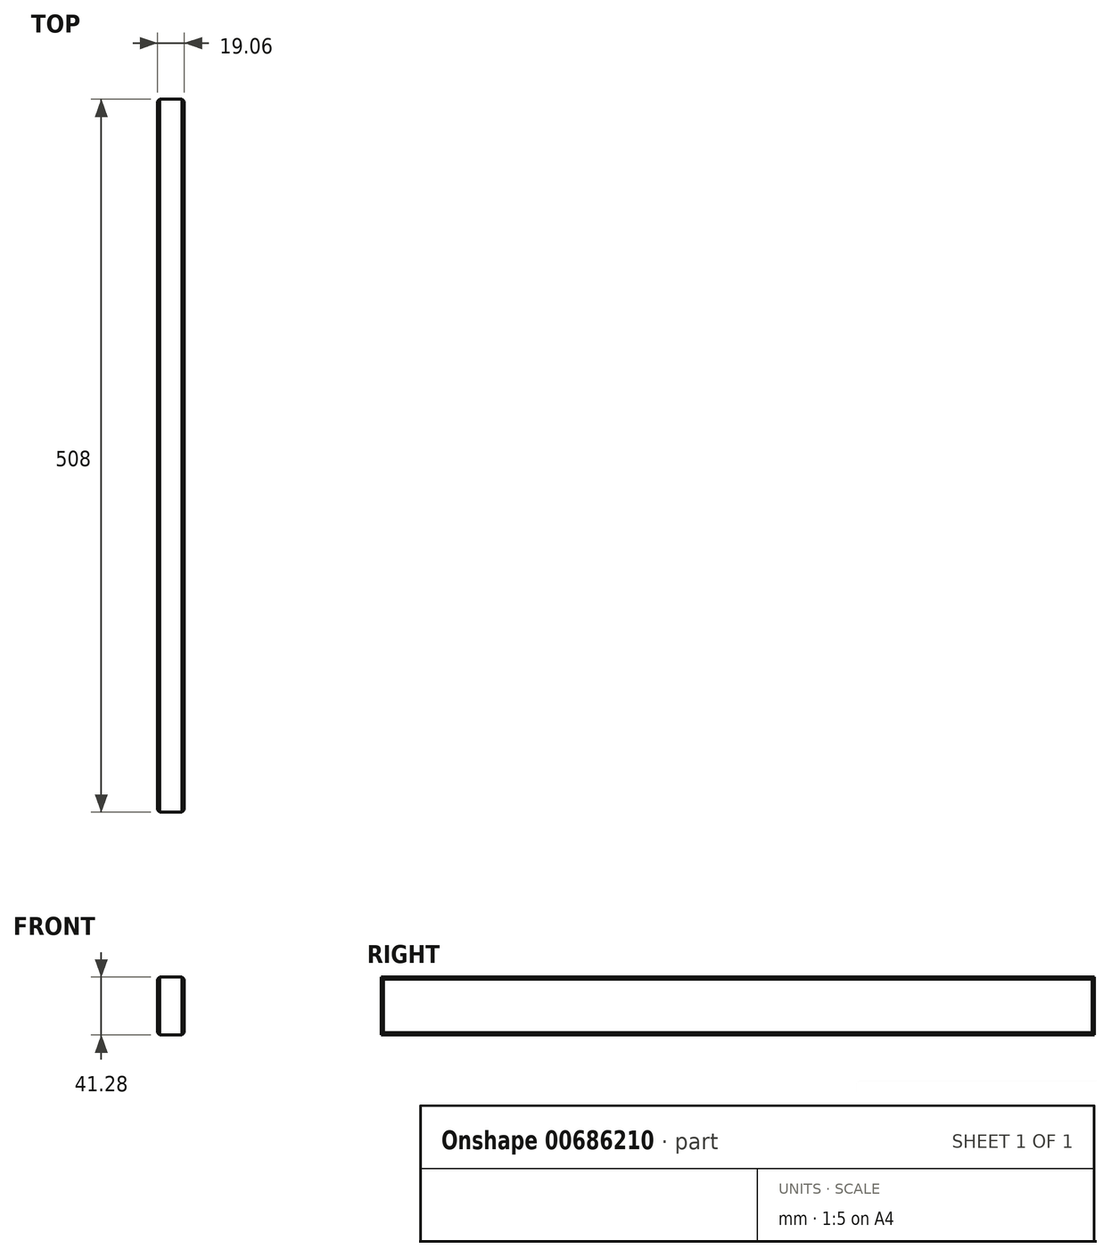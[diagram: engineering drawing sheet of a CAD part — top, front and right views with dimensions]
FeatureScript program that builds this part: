
annotation { "Feature Type Name" : "Feature", "Feature Type Description" : "" }
export const myFeature = defineFeature(function(context is Context, id is Id, definition is map)
    precondition{}
    {
        {
            var Q0;
            Q0=qCreatedBy(makeId("Front.planeOp"),FACE);
            var sketch = newSketch(context, id + "F0", { "sketchPlane" : qUnion([Q0])});
            skLineSegment(sketch, "E0.bottom", {"start": v(-9.52, 20.64) * mm, "end": v(9.53, 20.64) * mm});
            skLineSegment(sketch, "E0.top", {"start": v(-9.53, -20.64) * mm, "end": v(9.53, -20.64) * mm});
            skLineSegment(sketch, "E0.left", {"start": v(-9.52, 20.64) * mm, "end": v(-9.53, -20.64) * mm});
            skLineSegment(sketch, "E0.right", {"start": v(9.53, 20.64) * mm, "end": v(9.53, -20.64) * mm});
            skPoint(sketch, "E0.middle", {"position": v(0, 0) * mm});
            skSolve(sketch);
        }
        {
            var Q0;
            Q0=qSketchRegion(id+"F0",true);
            extrude(context, id + "F1", {"entities" : qUnion([Q0]), "endBound" : BoundingType.SYMMETRIC, "depth" : 508 * mm, "offsetDistance" : 25.4 * mm});
        }
        {
            var Q0;
            Q0=qCreatedBy(makeId("Right.planeOp"),FACE);
            var sketch = newSketch(context, id + "F2", { "sketchPlane" : qUnion([Q0])});
            skArc(sketch, "E1", {"start": v(-254, -17.46) * mm, "mid": v(0, -20.64) * mm, "end": v(254, -17.46) * mm});
            skPoint(sketch, "E2", {"position": v(-254, -17.46) * mm});
            skPoint(sketch, "E3", {"position": v(254, -17.46) * mm});
            skLineSegment(sketch, "E4", {"start": v(-254, -17.46) * mm, "end": v(-254, -21.27) * mm});
            skLineSegment(sketch, "E5", {"start": v(-254, -21.27) * mm, "end": v(254, -21.27) * mm});
            skLineSegment(sketch, "E6", {"start": v(254, -21.27) * mm, "end": v(254, -17.46) * mm});
            skSolve(sketch);
        }
        {
            var Q0;
            Q0=makeQuery(id+"F1.opExtrude","SWEPT_FACE",FACE,{"disambiguationData":[OSD([sQuery(id+"F0.wireOp",EDGE,"E0.left")])]});
            var Q1;
            Q1=makeQuery(id+"F1.opExtrude","SWEPT_FACE",FACE,{"disambiguationData":[OSD([sQuery(id+"F0.wireOp",EDGE,"E0.right")])]});
            chamfer(context, id + "F3", {"entities" : qUnion([Q0, Q1]), "width" : 1.59 * mm, "tangentPropagation" : true});
        }
    });
